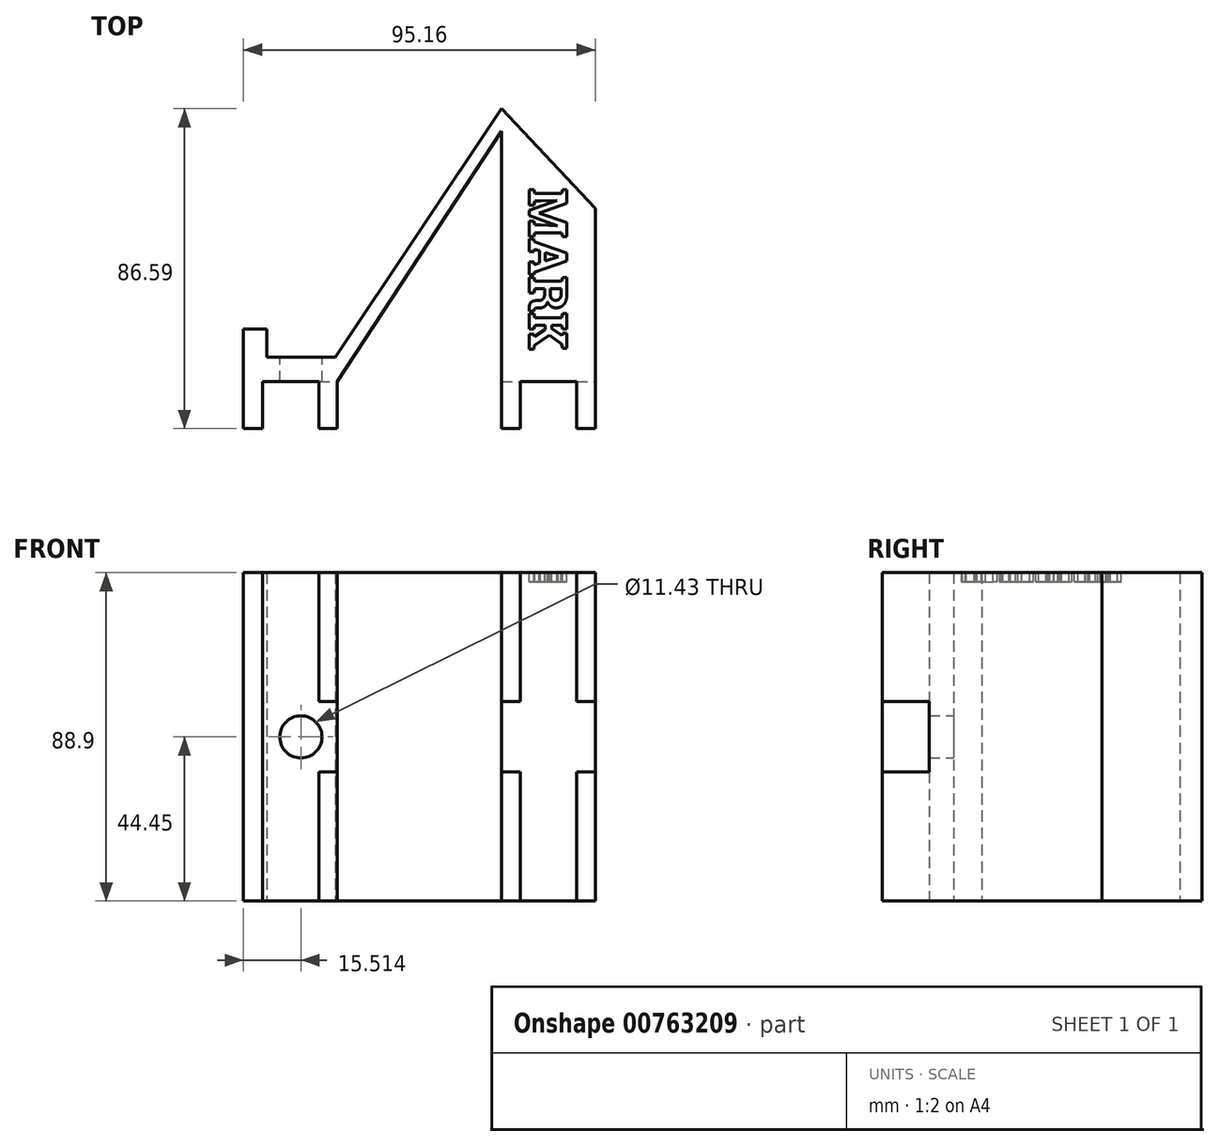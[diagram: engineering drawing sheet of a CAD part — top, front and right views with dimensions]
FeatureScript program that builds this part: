
annotation { "Feature Type Name" : "Feature", "Feature Type Description" : "" }
export const myFeature = defineFeature(function(context is Context, id is Id, definition is map)
    precondition{}
    {
        {
            var Q0;
            Q0=qCreatedBy(makeId("Top.planeOp"),FACE);
            var sketch = newSketch(context, id + "F0", { "sketchPlane" : qUnion([Q0])});
            skLineSegment(sketch, "E0.bottom", {"start": v(0, 0) * mm, "end": v(25.4, 0) * mm});
            skLineSegment(sketch, "E0.top", {"start": v(0, -46.85) * mm, "end": v(25.4, -46.85) * mm});
            skLineSegment(sketch, "E0.left", {"start": v(0, 0) * mm, "end": v(0, -46.85) * mm});
            skLineSegment(sketch, "E0.right", {"start": v(25.4, 0) * mm, "end": v(25.4, -46.85) * mm});
            skLineSegment(sketch, "E1", {"start": v(25.4, 0) * mm, "end": v(0, 27.04) * mm});
            skLineSegment(sketch, "E2", {"start": v(0, 27.04) * mm, "end": v(0, 0) * mm});
            skLineSegment(sketch, "E3", {"start": v(0, 27.04) * mm, "end": v(-49.44, -46.85) * mm});
            skLineSegment(sketch, "E4", {"start": v(-49.44, -46.85) * mm, "end": v(-44.36, -46.85) * mm});
            skLineSegment(sketch, "E5", {"start": v(-44.36, -46.85) * mm, "end": v(0, 21) * mm});
            skLineSegment(sketch, "E6", {"start": v(-45, -40.2) * mm, "end": v(-69.76, -40.2) * mm});
            skLineSegment(sketch, "E7", {"start": v(-69.76, -40.2) * mm, "end": v(-69.76, -46.85) * mm});
            skLineSegment(sketch, "E8", {"start": v(-69.76, -46.85) * mm, "end": v(-44.36, -46.85) * mm});
            skLineSegment(sketch, "E9", {"start": v(-69.76, -40.2) * mm, "end": v(-69.76, -32.58) * mm});
            skLineSegment(sketch, "E10", {"start": v(-69.76, -32.58) * mm, "end": v(-63.5, -32.58) * mm});
            skLineSegment(sketch, "E11", {"start": v(-63.5, -32.58) * mm, "end": v(-63.5, -40.2) * mm});
            skLineSegment(sketch, "E12", {"start": v(-69.76, -46.85) * mm, "end": v(-69.76, -59.55) * mm});
            skLineSegment(sketch, "E13", {"start": v(-69.76, -59.55) * mm, "end": v(-64.68, -59.55) * mm});
            skLineSegment(sketch, "E14", {"start": v(-64.68, -59.55) * mm, "end": v(-64.68, -46.85) * mm});
            skLineSegment(sketch, "E15", {"start": v(-49.44, -46.85) * mm, "end": v(-49.44, -59.55) * mm});
            skLineSegment(sketch, "E16", {"start": v(-49.44, -59.55) * mm, "end": v(-44.36, -59.55) * mm});
            skLineSegment(sketch, "E17", {"start": v(-44.36, -59.55) * mm, "end": v(-44.36, -46.85) * mm});
            skLineSegment(sketch, "E18", {"start": v(0, -46.85) * mm, "end": v(0, -59.55) * mm});
            skLineSegment(sketch, "E19", {"start": v(0, -59.55) * mm, "end": v(5.08, -59.55) * mm});
            skLineSegment(sketch, "E20", {"start": v(5.08, -59.55) * mm, "end": v(5.08, -46.85) * mm});
            skLineSegment(sketch, "E21", {"start": v(25.4, -59.55) * mm, "end": v(20.32, -59.55) * mm});
            skLineSegment(sketch, "E22", {"start": v(20.32, -59.55) * mm, "end": v(20.32, -46.85) * mm});
            skLineSegment(sketch, "E23", {"start": v(25.4, -59.55) * mm, "end": v(25.4, -46.85) * mm});
            skSolve(sketch);
        }
        {
            var Q0;
            Q0=qSketchRegion(id+"F0",true);
            extrude(context, id + "F1", {"entities" : qUnion([Q0]), "depth" : 88.9 * mm, "offsetDistance" : 25.4 * mm});
        }
        {
            var Q0;
            Q0=makeQuery(id+"F1.opExtrude","SWEPT_FACE",FACE,{"disambiguationData":[OSD([sQuery(id+"F0.wireOp",EDGE,"E6")])]});
            var sketch = newSketch(context, id + "F2", { "sketchPlane" : qUnion([Q0])});
            skLineSegment(sketch, "E24", {"start": v(45, 44.45) * mm, "end": v(63.5, 44.45) * mm, "construction": true});
            skLineSegment(sketch, "E25", {"start": v(54.25, 0) * mm, "end": v(54.25, 88.9) * mm, "construction": true});
            skCircle(sketch, "E26", {"center": v(54.25, 44.45) * mm, "radius": 5.72 * mm});
            skSolve(sketch);
        }
        {
            var Q0;
            Q0=qSketchRegion(id+"F2",true);
            extrude(context, id + "F3", {"entities" : qUnion([Q0]), "operationType" : NewBodyOperationType.REMOVE, "oppositeDirection" : true, "depth" : 7.62 * mm, "offsetDistance" : 25.4 * mm});
        }
        {
            var Q0;
            Q0=makeQuery(id+"F1.opExtrude","SWEPT_FACE",FACE,{"disambiguationData":[OSD([sQuery(id+"F0.wireOp",EDGE,"E0.right"),sQuery(id+"F0.wireOp",EDGE,"E23")])]});
            var sketch = newSketch(context, id + "F4", { "sketchPlane" : qUnion([Q0])});
            skPoint(sketch, "E27.startSnap0", {"position": v(0, 44.45) * mm});
            skLineSegment(sketch, "E28", {"start": v(-29.77, 88.9) * mm, "end": v(-29.77, 0) * mm, "construction": true});
            skLineSegment(sketch, "E29.bottom", {"start": v(-59.55, 53.98) * mm, "end": v(-46.85, 53.98) * mm});
            skLineSegment(sketch, "E29.top", {"start": v(-59.55, 34.93) * mm, "end": v(-46.85, 34.93) * mm});
            skLineSegment(sketch, "E29.left", {"start": v(-59.55, 53.98) * mm, "end": v(-59.55, 34.93) * mm});
            skLineSegment(sketch, "E29.right", {"start": v(-46.85, 53.98) * mm, "end": v(-46.85, 34.93) * mm});
            skPoint(sketch, "E30", {"position": v(-46.85, 44.45) * mm});
            skLineSegment(sketch, "E31", {"start": v(-59.55, 53.98) * mm, "end": v(-59.55, 88.9) * mm, "construction": true});
            skLineSegment(sketch, "E32", {"start": v(-59.55, 34.93) * mm, "end": v(-59.55, 0) * mm, "construction": true});
            skPoint(sketch, "E27.end.orphan", {"position": v(-59.55, 44.45) * mm});
            skPoint(sketch, "E27.start.orphan", {"position": v(-57.69, 44.45) * mm});
            skSolve(sketch);
        }
        {
            var Q0;
            Q0=makeQuery(id+"F4.imprint","IMPRINT",FACE,{"disambiguationData":[TD([[makeQuery(id+"F4.imprint","IMPRINT",EDGE,{"derivedFrom":sQuery(id+"F4.wireOp",EDGE,"E29.bottom")}),-1.0]])]});
            extrude(context, id + "F5", {"entities" : qUnion([Q0]), "operationType" : NewBodyOperationType.REMOVE, "oppositeDirection" : true, "depth" : 82.55 * mm, "offsetDistance" : 25.4 * mm});
        }
        {
            var Q0;
            Q0=makeQuery(id+"F1.opExtrude","CAP_FACE",FACE,{"disambiguationData":[OSD([sQuery(id+"F0.wireOp",EDGE,"E0.top"),sQuery(id+"F0.wireOp",EDGE,"E0.left"),sQuery(id+"F0.wireOp",EDGE,"E0.right"),sQuery(id+"F0.wireOp",EDGE,"E1"),sQuery(id+"F0.wireOp",EDGE,"E2"),sQuery(id+"F0.wireOp",EDGE,"E3"),sQuery(id+"F0.wireOp",EDGE,"E5"),sQuery(id+"F0.wireOp",EDGE,"E6"),sQuery(id+"F0.wireOp",EDGE,"E7"),sQuery(id+"F0.wireOp",EDGE,"E8"),sQuery(id+"F0.wireOp",EDGE,"E9"),sQuery(id+"F0.wireOp",EDGE,"E10"),sQuery(id+"F0.wireOp",EDGE,"E11"),sQuery(id+"F0.wireOp",EDGE,"E12"),sQuery(id+"F0.wireOp",EDGE,"E13"),sQuery(id+"F0.wireOp",EDGE,"E14"),sQuery(id+"F0.wireOp",EDGE,"E15"),sQuery(id+"F0.wireOp",EDGE,"E16"),sQuery(id+"F0.wireOp",EDGE,"E17"),sQuery(id+"F0.wireOp",EDGE,"E18"),sQuery(id+"F0.wireOp",EDGE,"E19"),sQuery(id+"F0.wireOp",EDGE,"E20"),sQuery(id+"F0.wireOp",EDGE,"E21"),sQuery(id+"F0.wireOp",EDGE,"E22"),sQuery(id+"F0.wireOp",EDGE,"E23")])],"isStart":false});
            var sketch = newSketch(context, id + "F6", { "sketchPlane" : qUnion([Q0])});
            skPoint(sketch, "E33", {"position": v(12.7, -16.66) * mm});
            skText(sketch, "E34", { "text": "MARK", "fontName": "RobotoSlab-Bold.ttf"});
            skLineSegment(sketch, "E35", {"start": v(12.7, -46.85) * mm, "end": v(12.7, 13.52) * mm, "construction": true});
            const initialGuessF6  = {"E34": [0.00755, 0.00556, 0, -1, 0.0103]};
            skSetInitialGuess(sketch, initialGuessF6);
            skSolve(sketch);
        }
        {
            var Q0;
            Q0=qSketchRegion(id+"F6",true);
            extrude(context, id + "F7", {"entities" : qUnion([Q0]), "operationType" : NewBodyOperationType.REMOVE, "oppositeDirection" : true, "depth" : 2.54 * mm, "offsetDistance" : 25.4 * mm});
        }
    });
